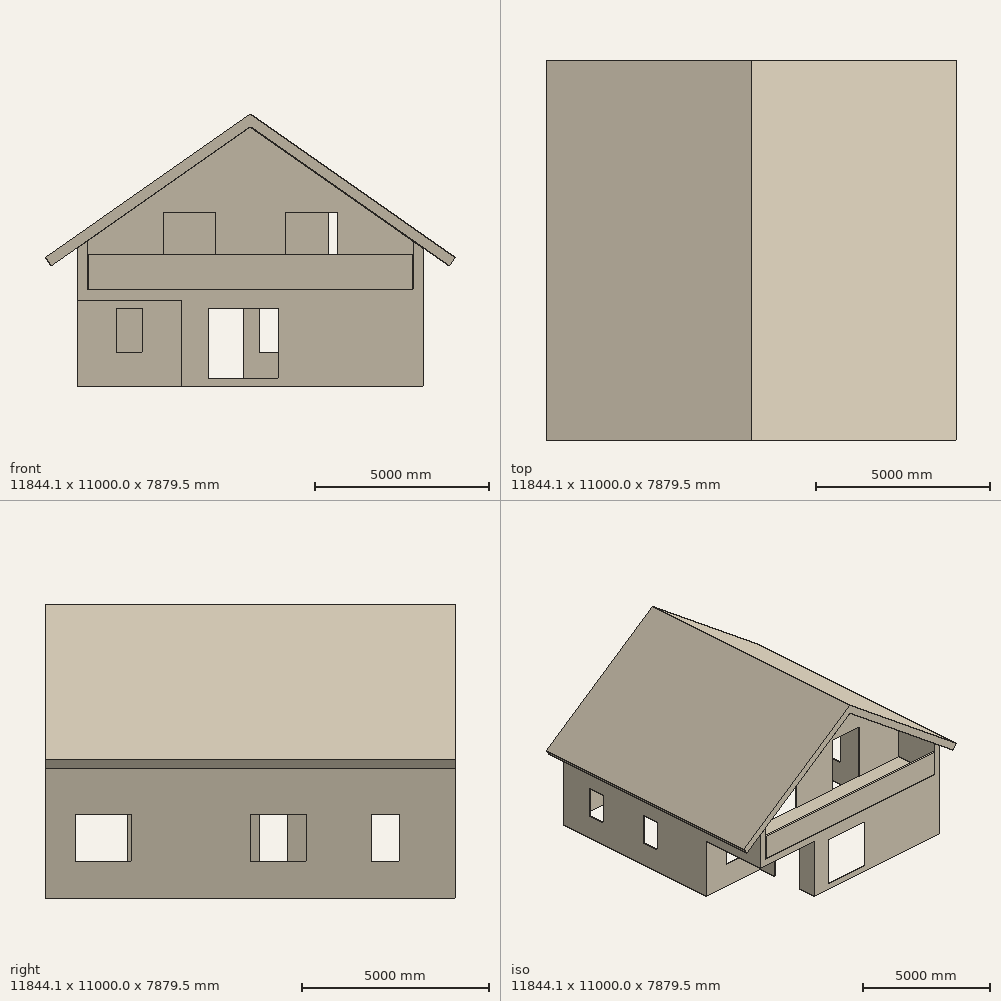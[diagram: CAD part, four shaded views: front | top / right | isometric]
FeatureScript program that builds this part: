
annotation { "Feature Type Name" : "Feature", "Feature Type Description" : "" }
export const myFeature = defineFeature(function(context is Context, id is Id, definition is map)
    precondition{}
    {
        {
            var Q0;
            Q0=qCreatedBy(makeId("Front.planeOp"),FACE);
            var sketch = newSketch(context, id + "F0", { "sketchPlane" : qUnion([Q0])});
            skLineSegment(sketch, "E0", {"start": v(-5000, 0) * mm, "end": v(5000, 0) * mm});
            skLineSegment(sketch, "E1", {"start": v(5000, 0) * mm, "end": v(5000, 4000) * mm});
            skLineSegment(sketch, "E2", {"start": v(5000, 4000) * mm, "end": v(0, 7501.04) * mm});
            skLineSegment(sketch, "E3", {"start": v(0, 7501.04) * mm, "end": v(-5000, 4000) * mm});
            skLineSegment(sketch, "E4", {"start": v(-5000, 4000) * mm, "end": v(-5000, 0) * mm});
            skSolve(sketch);
        }
        {
            var Q0;
            Q0 = qSketchRegion(id + "F0", true);
            extrude(context, id + "F1", {"entities" : qUnion([Q0]), "depth" : 5500 * mm, "offsetDistance" : 25 * mm, "hasSecondDirection" : true, "secondDirectionOppositeDirection" : true, "secondDirectionDepth" : 5500 * mm});
        }
        {
            var Q0;
            Q0=makeQuery(id+"F1.opExtrude","CAP_FACE",FACE,{"disambiguationData":[OSD([sQuery(id+"F0.wireOp",EDGE,"E0"),sQuery(id+"F0.wireOp",EDGE,"E1"),sQuery(id+"F0.wireOp",EDGE,"E2"),sQuery(id+"F0.wireOp",EDGE,"E3"),sQuery(id+"F0.wireOp",EDGE,"E4")])],"isStart":false});
            var sketch = newSketch(context, id + "F2", { "sketchPlane" : qUnion([Q0])});
            skLineSegment(sketch, "E5.bottom", {"start": v(-4700, 7501.04) * mm, "end": v(4700, 7501.04) * mm});
            skLineSegment(sketch, "E5.top", {"start": v(-4700, 2800) * mm, "end": v(4700, 2800) * mm});
            skLineSegment(sketch, "E5.left", {"start": v(-4700, 7501.04) * mm, "end": v(-4700, 2800) * mm});
            skLineSegment(sketch, "E5.right", {"start": v(4700, 7501.04) * mm, "end": v(4700, 2800) * mm});
            skLineSegment(sketch, "E6.bottom", {"start": v(-5000, 0) * mm, "end": v(-2000, 0) * mm});
            skLineSegment(sketch, "E6.top", {"start": v(-5000, 2500) * mm, "end": v(-2000, 2500) * mm});
            skLineSegment(sketch, "E6.left", {"start": v(-5000, 0) * mm, "end": v(-5000, 2500) * mm});
            skLineSegment(sketch, "E6.right", {"start": v(-2000, 0) * mm, "end": v(-2000, 2500) * mm});
            skSolve(sketch);
        }
        {
            var Q0;
            {var subQ5=sQuery(id+"F2.wireOp",EDGE,"E5.top");Q0=makeQuery(id+"F2.imprint","IMPRINT",FACE,{"disambiguationData":[TD([[makeQuery(id+"F2.imprint","IMPRINT",EDGE,{"derivedFrom":subQ5}),1.0]])]});}
            var Q1;
            Q1=makeQuery(id+"F2.imprint","IMPRINT",FACE,{"disambiguationData":[TD([[makeQuery(id+"F2.imprint","IMPRINT",EDGE,{"derivedFrom":sQuery(id+"F2.wireOp",EDGE,"E6.bottom")}),1.0]])]});
            extrude(context, id + "F3", {"entities" : qUnion([Q0, Q1]), "operationType" : NewBodyOperationType.REMOVE, "oppositeDirection" : true, "depth" : 2000 * mm, "offsetDistance" : 25 * mm});
        }
        {
            var Q0;
            Q0=qCreatedBy(makeId("Front.planeOp"),FACE);
            var sketch = newSketch(context, id + "F4", { "sketchPlane" : qUnion([Q0])});
            skLineSegment(sketch, "E7.0", {"start": v(0, 7501.04) * mm, "end": v(-4700, 4210.06) * mm});
            skLineSegment(sketch, "E8.0", {"start": v(4700, 4210.06) * mm, "end": v(0, 7501.04) * mm});
            skLineSegment(sketch, "E9", {"start": v(-5750, 3487.05) * mm, "end": v(0, 7513.25) * mm});
            skLineSegment(sketch, "E10", {"start": v(0, 7513.25) * mm, "end": v(5750, 3487.05) * mm});
            skLineSegment(sketch, "E11", {"start": v(5750, 3487.05) * mm, "end": v(5922.07, 3732.8) * mm});
            skLineSegment(sketch, "E12", {"start": v(5922.07, 3732.8) * mm, "end": v(0, 7879.48) * mm});
            skLineSegment(sketch, "E13", {"start": v(0, 7879.48) * mm, "end": v(-5922.07, 3732.8) * mm});
            skLineSegment(sketch, "E14", {"start": v(-5922.07, 3732.8) * mm, "end": v(-5750, 3487.05) * mm});
            skSolve(sketch);
        }
        {
            var Q0;
            Q0=makeQuery(id+"F4.imprint","IMPRINT",FACE,{"disambiguationData":[TD([[makeQuery(id+"F4.imprint","IMPRINT",EDGE,{"derivedFrom":sQuery(id+"F4.wireOp",EDGE,"E9")}),1.0]])]});
            extrude(context, id + "F5", {"entities" : qUnion([Q0]), "depth" : 5500 * mm, "offsetDistance" : 25 * mm, "hasSecondDirection" : true, "secondDirectionOppositeDirection" : true, "secondDirectionDepth" : 5500 * mm});
        }
        {
            var Q0;
            Q0=makeQuery(id+"F3.boolean.opBoolean","COPY",FACE,{"derivedFrom":makeQuery(id+"F3.opExtrude","CAP_FACE",FACE,{"disambiguationData":[OSD([sQuery(id+"F2.wireOp",EDGE,"E6.bottom"),sQuery(id+"F2.wireOp",EDGE,"E6.top"),sQuery(id+"F2.wireOp",EDGE,"E6.left"),sQuery(id+"F2.wireOp",EDGE,"E6.right")])],"isStart":false})});
            var sketch = newSketch(context, id + "F6", { "sketchPlane" : qUnion([Q0])});
            skLineSegment(sketch, "E15.0.0", {"start": v(-5000, 0) * mm, "end": v(-2000, 0) * mm});
            skLineSegment(sketch, "E15.0.1", {"start": v(-2000, 0) * mm, "end": v(-2000, 2500) * mm});
            skLineSegment(sketch, "E15.0.2", {"start": v(-2000, 2500) * mm, "end": v(-5000, 2500) * mm});
            skLineSegment(sketch, "E15.0.3", {"start": v(-5000, 2500) * mm, "end": v(-5000, 0) * mm});
            skSolve(sketch);
        }
        {
            var Q0;
            Q0=makeQuery(id+"F6.imprint","IMPRINT",FACE,{"disambiguationData":[TD([[makeQuery(id+"F6.imprint","IMPRINT",EDGE,{"derivedFrom":sQuery(id+"F6.wireOp",EDGE,"E15.0.0")}),1.0]])]});
            extrude(context, id + "F7", {"entities" : qUnion([Q0]), "operationType" : NewBodyOperationType.REMOVE, "oppositeDirection" : true, "depth" : 1000 * mm, "offsetDistance" : 25 * mm});
        }
        {
            var Q0;
            Q0=makeQuery(id+"F1.opExtrude","SWEPT_FACE",FACE,{"disambiguationData":[OSD([sQuery(id+"F0.wireOp",EDGE,"E0")])]});
            shell(context, id + "F8", {"entities" : qUnion([Q0]), "thickness" : 30 * mm});
        }
        {
            var Q0;
            Q0=makeQuery(id+"F3.boolean.opBoolean","COPY",FACE,{"derivedFrom":makeQuery(id+"F3.opExtrude","CAP_FACE",FACE,{"disambiguationData":[OSD([sQuery(id+"F0.wireOp",EDGE,"E2"),sQuery(id+"F0.wireOp",EDGE,"E3"),sQuery(id+"F2.wireOp",EDGE,"E5.top"),sQuery(id+"F2.wireOp",EDGE,"E5.left"),sQuery(id+"F2.wireOp",EDGE,"E5.right")])],"isStart":false})});
            var sketch = newSketch(context, id + "F9", { "sketchPlane" : qUnion([Q0])});
            skLineSegment(sketch, "E16.bottom", {"start": v(-1000, 2800) * mm, "end": v(-2500, 2800) * mm});
            skLineSegment(sketch, "E16.top", {"start": v(-1000, 5050) * mm, "end": v(-2500, 5050) * mm});
            skLineSegment(sketch, "E16.left", {"start": v(-1000, 2800) * mm, "end": v(-1000, 5050) * mm});
            skLineSegment(sketch, "E16.right", {"start": v(-2500, 2800) * mm, "end": v(-2500, 5050) * mm});
            skLineSegment(sketch, "E17.bottom", {"start": v(1000, 2800) * mm, "end": v(2500, 2800) * mm});
            skLineSegment(sketch, "E17.top", {"start": v(1000, 5050) * mm, "end": v(2500, 5050) * mm});
            skLineSegment(sketch, "E17.left", {"start": v(1000, 2800) * mm, "end": v(1000, 5050) * mm});
            skLineSegment(sketch, "E17.right", {"start": v(2500, 2800) * mm, "end": v(2500, 5050) * mm});
            skSolve(sketch);
        }
        {
            var Q0;
            Q0=makeQuery(id+"F9.imprint","IMPRINT",FACE,{"disambiguationData":[TD([[makeQuery(id+"F9.imprint","IMPRINT",EDGE,{"derivedFrom":sQuery(id+"F9.wireOp",EDGE,"E16.bottom")}),1.0]])]});
            var Q1;
            Q1=makeQuery(id+"F9.imprint","IMPRINT",FACE,{"disambiguationData":[TD([[makeQuery(id+"F9.imprint","IMPRINT",EDGE,{"derivedFrom":sQuery(id+"F9.wireOp",EDGE,"E17.bottom")}),1.0]])]});
            extrude(context, id + "F10", {"entities" : qUnion([Q0, Q1]), "operationType" : NewBodyOperationType.REMOVE, "endBound" : BoundingType.UP_TO_NEXT, "oppositeDirection" : true, "depth" : 25 * mm, "offsetDistance" : 25 * mm});
        }
        {
            var Q0;
            Q0=makeQuery(id+"F3.boolean.opBoolean","COPY",FACE,{"derivedFrom":makeQuery(id+"F3.opExtrude","SWEPT_FACE",FACE,{"disambiguationData":[OSD([sQuery(id+"F2.wireOp",EDGE,"E6.right")])]})});
            var sketch = newSketch(context, id + "F11", { "sketchPlane" : qUnion([Q0])});
            skLineSegment(sketch, "E18.bottom", {"start": v(4700, 0) * mm, "end": v(3300, 0) * mm});
            skLineSegment(sketch, "E18.top", {"start": v(4700, 2250) * mm, "end": v(3300, 2250) * mm});
            skLineSegment(sketch, "E18.left", {"start": v(4700, 0) * mm, "end": v(4700, 2250) * mm});
            skLineSegment(sketch, "E18.right", {"start": v(3300, 0) * mm, "end": v(3300, 2250) * mm});
            skSolve(sketch);
        }
        {
            var Q0;
            Q0=makeQuery(id+"F11.imprint","IMPRINT",FACE,{"disambiguationData":[TD([[makeQuery(id+"F11.imprint","IMPRINT",EDGE,{"derivedFrom":sQuery(id+"F11.wireOp",EDGE,"E18.bottom")}),1.0]])]});
            extrude(context, id + "F12", {"entities" : qUnion([Q0]), "operationType" : NewBodyOperationType.REMOVE, "endBound" : BoundingType.UP_TO_NEXT, "oppositeDirection" : true, "depth" : 25 * mm, "offsetDistance" : 25 * mm});
        }
        {
            var Q0;
            Q0=makeQuery(id+"F1.opExtrude","CAP_FACE",FACE,{"disambiguationData":[OSD([sQuery(id+"F0.wireOp",EDGE,"E0"),sQuery(id+"F0.wireOp",EDGE,"E1"),sQuery(id+"F0.wireOp",EDGE,"E2"),sQuery(id+"F0.wireOp",EDGE,"E3"),sQuery(id+"F0.wireOp",EDGE,"E4")])],"isStart":false});
            var sketch = newSketch(context, id + "F13", { "sketchPlane" : qUnion([Q0])});
            skLineSegment(sketch, "E19.bottom", {"start": v(-1200, 2250) * mm, "end": v(800, 2250) * mm});
            skLineSegment(sketch, "E19.top", {"start": v(-1200, 250) * mm, "end": v(800, 250) * mm});
            skLineSegment(sketch, "E19.left", {"start": v(-1200, 2250) * mm, "end": v(-1200, 250) * mm});
            skLineSegment(sketch, "E19.right", {"start": v(800, 2250) * mm, "end": v(800, 250) * mm});
            skSolve(sketch);
        }
        {
            var Q0;
            Q0=makeQuery(id+"F13.imprint","IMPRINT",FACE,{"disambiguationData":[TD([[makeQuery(id+"F13.imprint","IMPRINT",EDGE,{"derivedFrom":sQuery(id+"F13.wireOp",EDGE,"E19.bottom")}),-1.0]])]});
            var Q1;
            Q1=makeQuery(id+"F13.imprint","IMPRINT",FACE,{"disambiguationData":[TD([[makeQuery(id+"F13.imprint","IMPRINT",EDGE,{"derivedFrom":sQuery(id+"F13.wireOp",EDGE,"Z1fPz6J2-dJBs-qAqv-utnJ-TbpYLxqEym8b.bottom")}),-1.0]])]});
            extrude(context, id + "F14", {"entities" : qUnion([Q0, Q1]), "operationType" : NewBodyOperationType.REMOVE, "endBound" : BoundingType.UP_TO_NEXT, "oppositeDirection" : true, "depth" : 25 * mm, "offsetDistance" : 25 * mm});
        }
        {
            var Q0;
            Q0=makeQuery(id+"F1.opExtrude","SWEPT_FACE",FACE,{"disambiguationData":[OSD([sQuery(id+"F0.wireOp",EDGE,"E1")])]});
            var sketch = newSketch(context, id + "F15", { "sketchPlane" : qUnion([Q0])});
            skLineSegment(sketch, "E20.bottom", {"start": v(-4700, 2250) * mm, "end": v(-3200, 2250) * mm});
            skLineSegment(sketch, "E20.top", {"start": v(-4700, 1000) * mm, "end": v(-3200, 1000) * mm});
            skLineSegment(sketch, "E20.left", {"start": v(-4700, 2250) * mm, "end": v(-4700, 1000) * mm});
            skLineSegment(sketch, "E20.right", {"start": v(-3200, 2250) * mm, "end": v(-3200, 1000) * mm});
            skLineSegment(sketch, "E21.bottom", {"start": v(0, 2250) * mm, "end": v(1500, 2250) * mm});
            skLineSegment(sketch, "E21.top", {"start": v(0, 1000) * mm, "end": v(1500, 1000) * mm});
            skLineSegment(sketch, "E21.left", {"start": v(0, 2250) * mm, "end": v(0, 1000) * mm});
            skLineSegment(sketch, "E21.right", {"start": v(1500, 2250) * mm, "end": v(1500, 1000) * mm});
            skLineSegment(sketch, "E22.bottom", {"start": v(3250, 2250) * mm, "end": v(4000, 2250) * mm});
            skLineSegment(sketch, "E22.top", {"start": v(3250, 1000) * mm, "end": v(4000, 1000) * mm});
            skLineSegment(sketch, "E22.left", {"start": v(3250, 2250) * mm, "end": v(3250, 1000) * mm});
            skLineSegment(sketch, "E22.right", {"start": v(4000, 2250) * mm, "end": v(4000, 1000) * mm});
            skSolve(sketch);
        }
        {
            var Q0;
            Q0=makeQuery(id+"F15.imprint","IMPRINT",FACE,{"disambiguationData":[TD([[makeQuery(id+"F15.imprint","IMPRINT",EDGE,{"derivedFrom":sQuery(id+"F15.wireOp",EDGE,"E20.bottom")}),-1.0]])]});
            var Q1;
            Q1=makeQuery(id+"F15.imprint","IMPRINT",FACE,{"disambiguationData":[TD([[makeQuery(id+"F15.imprint","IMPRINT",EDGE,{"derivedFrom":sQuery(id+"F15.wireOp",EDGE,"E21.bottom")}),-1.0]])]});
            var Q2;
            Q2=makeQuery(id+"F15.imprint","IMPRINT",FACE,{"disambiguationData":[TD([[makeQuery(id+"F15.imprint","IMPRINT",EDGE,{"derivedFrom":sQuery(id+"F15.wireOp",EDGE,"E22.bottom")}),-1.0]])]});
            extrude(context, id + "F16", {"entities" : qUnion([Q0, Q1, Q2]), "operationType" : NewBodyOperationType.REMOVE, "endBound" : BoundingType.UP_TO_NEXT, "oppositeDirection" : true, "depth" : 25 * mm, "offsetDistance" : 25 * mm});
        }
        {
            var Q0;
            Q0=makeQuery(id+"F1.opExtrude","CAP_FACE",FACE,{"disambiguationData":[OSD([sQuery(id+"F0.wireOp",EDGE,"E0"),sQuery(id+"F0.wireOp",EDGE,"E1"),sQuery(id+"F0.wireOp",EDGE,"E2"),sQuery(id+"F0.wireOp",EDGE,"E3"),sQuery(id+"F0.wireOp",EDGE,"E4")])],"isStart":false});
            var sketch = newSketch(context, id + "F17", { "sketchPlane" : qUnion([Q0])});
            skLineSegment(sketch, "E23.bottom", {"start": v(-4690, 3810) * mm, "end": v(4690, 3810) * mm});
            skLineSegment(sketch, "E23.top", {"start": v(-4690, 2810) * mm, "end": v(4690, 2810) * mm});
            skLineSegment(sketch, "E23.left", {"start": v(-4690, 3810) * mm, "end": v(-4690, 2810) * mm});
            skLineSegment(sketch, "E23.right", {"start": v(4690, 3810) * mm, "end": v(4690, 2810) * mm});
            skSolve(sketch);
        }
        {
            var Q0;
            Q0=makeQuery(id+"F17.imprint","IMPRINT",FACE,{"disambiguationData":[TD([[makeQuery(id+"F17.imprint","IMPRINT",EDGE,{"derivedFrom":sQuery(id+"F17.wireOp",EDGE,"E23.bottom")}),-1.0]])]});
            extrude(context, id + "F18", {"entities" : qUnion([Q0]), "oppositeDirection" : true, "depth" : 100 * mm, "offsetDistance" : 25 * mm});
        }
        {
            var Q0;
            Q0=makeQuery(id+"F7.boolean.opBoolean","COPY",FACE,{"derivedFrom":makeQuery(id+"F7.opExtrude","CAP_FACE",FACE,{"disambiguationData":[OSD([sQuery(id+"F6.wireOp",EDGE,"E15.0.0"),sQuery(id+"F6.wireOp",EDGE,"E15.0.1"),sQuery(id+"F6.wireOp",EDGE,"E15.0.2"),sQuery(id+"F6.wireOp",EDGE,"E15.0.3")])],"isStart":false})});
            var sketch = newSketch(context, id + "F19", { "sketchPlane" : qUnion([Q0])});
            skLineSegment(sketch, "E24.bottom", {"start": v(-3875, 2250) * mm, "end": v(-3125, 2250) * mm});
            skLineSegment(sketch, "E24.top", {"start": v(-3875, 1000) * mm, "end": v(-3125, 1000) * mm});
            skLineSegment(sketch, "E24.left", {"start": v(-3875, 2250) * mm, "end": v(-3875, 1000) * mm});
            skLineSegment(sketch, "E24.right", {"start": v(-3125, 2250) * mm, "end": v(-3125, 1000) * mm});
            skSolve(sketch);
        }
        {
            var Q0;
            Q0=makeQuery(id+"F19.imprint","IMPRINT",FACE,{"disambiguationData":[TD([[makeQuery(id+"F19.imprint","IMPRINT",EDGE,{"derivedFrom":sQuery(id+"F19.wireOp",EDGE,"E24.bottom")}),-1.0]])]});
            extrude(context, id + "F20", {"entities" : qUnion([Q0]), "operationType" : NewBodyOperationType.REMOVE, "endBound" : BoundingType.UP_TO_NEXT, "oppositeDirection" : true, "depth" : 25 * mm, "offsetDistance" : 25 * mm});
        }
        {
            var Q0;
            Q0=makeQuery(id+"F1.opExtrude","CAP_FACE",FACE,{"disambiguationData":[OSD([sQuery(id+"F0.wireOp",EDGE,"E0"),sQuery(id+"F0.wireOp",EDGE,"E1"),sQuery(id+"F0.wireOp",EDGE,"E2"),sQuery(id+"F0.wireOp",EDGE,"E3"),sQuery(id+"F0.wireOp",EDGE,"E4")])],"isStart":true});
            var sketch = newSketch(context, id + "F21", { "sketchPlane" : qUnion([Q0])});
            skLineSegment(sketch, "E25.bottom", {"start": v(-3000, 2250) * mm, "end": v(-2250, 2250) * mm});
            skLineSegment(sketch, "E25.top", {"start": v(-3000, 1000) * mm, "end": v(-2250, 1000) * mm});
            skLineSegment(sketch, "E25.left", {"start": v(-3000, 2250) * mm, "end": v(-3000, 1000) * mm});
            skLineSegment(sketch, "E25.right", {"start": v(-2250, 2250) * mm, "end": v(-2250, 1000) * mm});
            skLineSegment(sketch, "E26.bottom", {"start": v(-1000, 2250) * mm, "end": v(-250, 2250) * mm});
            skLineSegment(sketch, "E26.top", {"start": v(-1000, 1000) * mm, "end": v(-250, 1000) * mm});
            skLineSegment(sketch, "E26.left", {"start": v(-1000, 2250) * mm, "end": v(-1000, 1000) * mm});
            skLineSegment(sketch, "E26.right", {"start": v(-250, 2250) * mm, "end": v(-250, 1000) * mm});
            skLineSegment(sketch, "E27.bottom", {"start": v(200, 0) * mm, "end": v(1200, 0) * mm});
            skLineSegment(sketch, "E27.top", {"start": v(200, 2250) * mm, "end": v(1200, 2250) * mm});
            skLineSegment(sketch, "E27.left", {"start": v(200, 0) * mm, "end": v(200, 2250) * mm});
            skLineSegment(sketch, "E27.right", {"start": v(1200, 0) * mm, "end": v(1200, 2250) * mm});
            skLineSegment(sketch, "E28.bottom", {"start": v(-3000, 5050) * mm, "end": v(-2250, 5050) * mm});
            skLineSegment(sketch, "E28.top", {"start": v(-3000, 3800) * mm, "end": v(-2250, 3800) * mm});
            skLineSegment(sketch, "E28.left", {"start": v(-3000, 5050) * mm, "end": v(-3000, 3800) * mm});
            skLineSegment(sketch, "E28.right", {"start": v(-2250, 5050) * mm, "end": v(-2250, 3800) * mm});
            skLineSegment(sketch, "E29.bottom", {"start": v(-1000, 5050) * mm, "end": v(-250, 5050) * mm});
            skLineSegment(sketch, "E29.top", {"start": v(-1000, 3800) * mm, "end": v(-250, 3800) * mm});
            skLineSegment(sketch, "E29.left", {"start": v(-1000, 5050) * mm, "end": v(-1000, 3800) * mm});
            skLineSegment(sketch, "E29.right", {"start": v(-250, 5050) * mm, "end": v(-250, 3800) * mm});
            skLineSegment(sketch, "E30.bottom", {"start": v(2500, 5050) * mm, "end": v(3250, 5050) * mm});
            skLineSegment(sketch, "E30.top", {"start": v(2500, 3800) * mm, "end": v(3250, 3800) * mm});
            skLineSegment(sketch, "E30.left", {"start": v(2500, 5050) * mm, "end": v(2500, 3800) * mm});
            skLineSegment(sketch, "E30.right", {"start": v(3250, 5050) * mm, "end": v(3250, 3800) * mm});
            skSolve(sketch);
        }
        {
            var Q0;
            Q0=makeQuery(id+"F21.imprint","IMPRINT",FACE,{"disambiguationData":[TD([[makeQuery(id+"F21.imprint","IMPRINT",EDGE,{"derivedFrom":sQuery(id+"F21.wireOp",EDGE,"E25.bottom")}),-1.0]])]});
            var Q1;
            Q1=makeQuery(id+"F21.imprint","IMPRINT",FACE,{"disambiguationData":[TD([[makeQuery(id+"F21.imprint","IMPRINT",EDGE,{"derivedFrom":sQuery(id+"F21.wireOp",EDGE,"E26.bottom")}),-1.0]])]});
            var Q2;
            Q2=makeQuery(id+"F21.imprint","IMPRINT",FACE,{"disambiguationData":[TD([[makeQuery(id+"F21.imprint","IMPRINT",EDGE,{"derivedFrom":sQuery(id+"F21.wireOp",EDGE,"E27.bottom")}),-1.0]])]});
            var Q3;
            Q3=makeQuery(id+"F21.imprint","IMPRINT",FACE,{"disambiguationData":[TD([[makeQuery(id+"F21.imprint","IMPRINT",EDGE,{"derivedFrom":sQuery(id+"F21.wireOp",EDGE,"E28.bottom")}),-1.0]])]});
            var Q4;
            Q4=makeQuery(id+"F21.imprint","IMPRINT",FACE,{"disambiguationData":[TD([[makeQuery(id+"F21.imprint","IMPRINT",EDGE,{"derivedFrom":sQuery(id+"F21.wireOp",EDGE,"E29.bottom")}),-1.0]])]});
            var Q5;
            Q5=makeQuery(id+"F21.imprint","IMPRINT",FACE,{"disambiguationData":[TD([[makeQuery(id+"F21.imprint","IMPRINT",EDGE,{"derivedFrom":sQuery(id+"F21.wireOp",EDGE,"E30.bottom")}),-1.0]])]});
            extrude(context, id + "F22", {"entities" : qUnion([Q0, Q1, Q2, Q3, Q4, Q5]), "operationType" : NewBodyOperationType.REMOVE, "endBound" : BoundingType.UP_TO_NEXT, "oppositeDirection" : true, "depth" : 25 * mm, "offsetDistance" : 25 * mm});
        }
        {
            var Q0;
            Q0=makeQuery(id+"F1.opExtrude","SWEPT_FACE",FACE,{"disambiguationData":[OSD([sQuery(id+"F0.wireOp",EDGE,"E4")])]});
            var sketch = newSketch(context, id + "F23", { "sketchPlane" : qUnion([Q0])});
            skLineSegment(sketch, "E31.bottom", {"start": v(-4000, 2250) * mm, "end": v(-3250, 2250) * mm});
            skLineSegment(sketch, "E31.top", {"start": v(-4000, 1000) * mm, "end": v(-3250, 1000) * mm});
            skLineSegment(sketch, "E31.left", {"start": v(-4000, 2250) * mm, "end": v(-4000, 1000) * mm});
            skLineSegment(sketch, "E31.right", {"start": v(-3250, 2250) * mm, "end": v(-3250, 1000) * mm});
            skLineSegment(sketch, "E32.bottom", {"start": v(-1000, 2250) * mm, "end": v(-250, 2250) * mm});
            skLineSegment(sketch, "E32.top", {"start": v(-1000, 1000) * mm, "end": v(-250, 1000) * mm});
            skLineSegment(sketch, "E32.left", {"start": v(-1000, 2250) * mm, "end": v(-1000, 1000) * mm});
            skLineSegment(sketch, "E32.right", {"start": v(-250, 2250) * mm, "end": v(-250, 1000) * mm});
            skSolve(sketch);
        }
        {
            var Q0;
            Q0=makeQuery(id+"F23.imprint","IMPRINT",FACE,{"disambiguationData":[TD([[makeQuery(id+"F23.imprint","IMPRINT",EDGE,{"derivedFrom":sQuery(id+"F23.wireOp",EDGE,"E31.bottom")}),-1.0]])]});
            var Q1;
            Q1=makeQuery(id+"F23.imprint","IMPRINT",FACE,{"disambiguationData":[TD([[makeQuery(id+"F23.imprint","IMPRINT",EDGE,{"derivedFrom":sQuery(id+"F23.wireOp",EDGE,"E32.bottom")}),-1.0]])]});
            extrude(context, id + "F24", {"entities" : qUnion([Q0, Q1]), "operationType" : NewBodyOperationType.REMOVE, "endBound" : BoundingType.UP_TO_NEXT, "oppositeDirection" : true, "depth" : 25 * mm, "offsetDistance" : 25 * mm});
        }
    });
